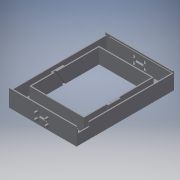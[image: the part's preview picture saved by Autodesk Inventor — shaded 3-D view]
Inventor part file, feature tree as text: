
AUTODESK INVENTOR PART (.ipt)
format: ipt  version: 2018.3 (Build 223284000, 284)  size: 390,144 bytes
history: native  units: mm
features: extrude x10, sketch x10, chamfer x2
ambient origin geometry x8: Origin, YZ Plane, XZ Plane, XY Plane, X Axis, Y Axis, Z Axis, Center Point
bodies: Solid1 (feature_tree)
feature tree (22):
  extrude  "Extrusion1"  Depth=130.0mm
  extrude  "Extrusion2"  Depth=90.0mm
  extrude  "Extrusion3"  TaperAngle=210.0deg  [1 undecoded]
  extrude  "Extrusion4"  Depth=2.1mm
  chamfer  "Chamfer1"  Distance=2.1mm
  extrude  "Extrusion5"  Depth=3.1mm
  chamfer  "Chamfer2"  Distance=2.1mm
  extrude  "Extrusion6"  Depth=20.0mm
  extrude  "Extrusion7"  Depth=20.0mm
  extrude  "Extrusion15"  Depth=3.0mm
  extrude  "Extrusion16"  Depth=85.0mm
  extrude  "Extrusion17"  Depth=85.0mm
  sketch  "Sketch1"  dims[d0=90.0mm d1=130.0mm]
  sketch  "Sketch2"  dims[d2=70.0mm d3=90.0mm]
  sketch  "Sketch3"  dims[d4=20.0mm d5=0.0mm d6=210.0deg]
  sketch  "Sketch4"  dims[d7=3.1mm d8=26.471143mm d9=2.1mm d10=0.0mm]
  sketch  "Sketch5"  dims[d11=30.0deg d12=3.1mm]
  sketch  "Sketch6"  dims[d13=26.471143mm d14=2.1mm d15=0.0mm]
  sketch  "Sketch7"  dims[d16=20.0mm d17=20.0mm]
  sketch  "Sketch16"  dims[d18=10.0mm d19=20.0mm]
  sketch  "Sketch17"  dims[d20=14.0mm d21=3.0mm]
  sketch  "Sketch18"  dims[d22=3.0mm d23=35.0mm d24=35.0mm d25=1.45mm d26=1.45mm d27=1.1mm d28=1.1mm d29=12.11mm d30=1.13mm d31=1.13mm d32=4.83mm d33=4.83mm d34=1.129mm d35=1.128692mm d36=4.0mm d37=0.0mm d38=0.5mm d39=2.0mm d40=45.0deg d41=20.0mm d42=14.0mm d43=3.0mm d44=3.0mm d45=35.0mm d46=35.0mm d74=4.0mm d75=0.0mm d76=0.5mm d77=2.0mm d78=45.0deg d79=128.5mm d80=87.0mm d81=127.0mm d82=46.0mm d83=2.0mm d84=16.434mm d85=2.0mm d86=30.566mm d87=73.0mm d88=2.0mm d89=18.0mm d90=0.0mm d100=11.0mm d101=2.6mm d102=8.7mm d103=39.5mm d104=39.5mm d105=8.7mm d106=10.0mm d107=0.0mm d142=2.4mm d144=2.4mm d148=2.4mm d151=4.44678mm d154=2.4mm d158=11.89mm d159=11.0mm d160=2.6mm d161=4.5mm d162=5.7mm d164=2.87mm d165=2.93mm d168=14.29mm d170=8.14mm d172=2.93mm d173=8.14mm d174=4.44678mm d175=0.697749mm d176=1.128969mm d177=14.29mm d178=2.0mm d179=15.0mm d180=14.282965mm d181=10.0mm d182=0.0mm d183=2.8mm d184=0.0mm d185=1.5mm d186=0.8mm d187=1.25mm d188=0.05mm d189=1.5mm d190=0.8mm d191=1.25mm d192=85.0mm d193=0.0mm]
note: 1 required parameter value undecoded (feature->parameter linkage not recoverable at this tier; creation-order binding heuristic only, values carry confidence <= 0.55)
